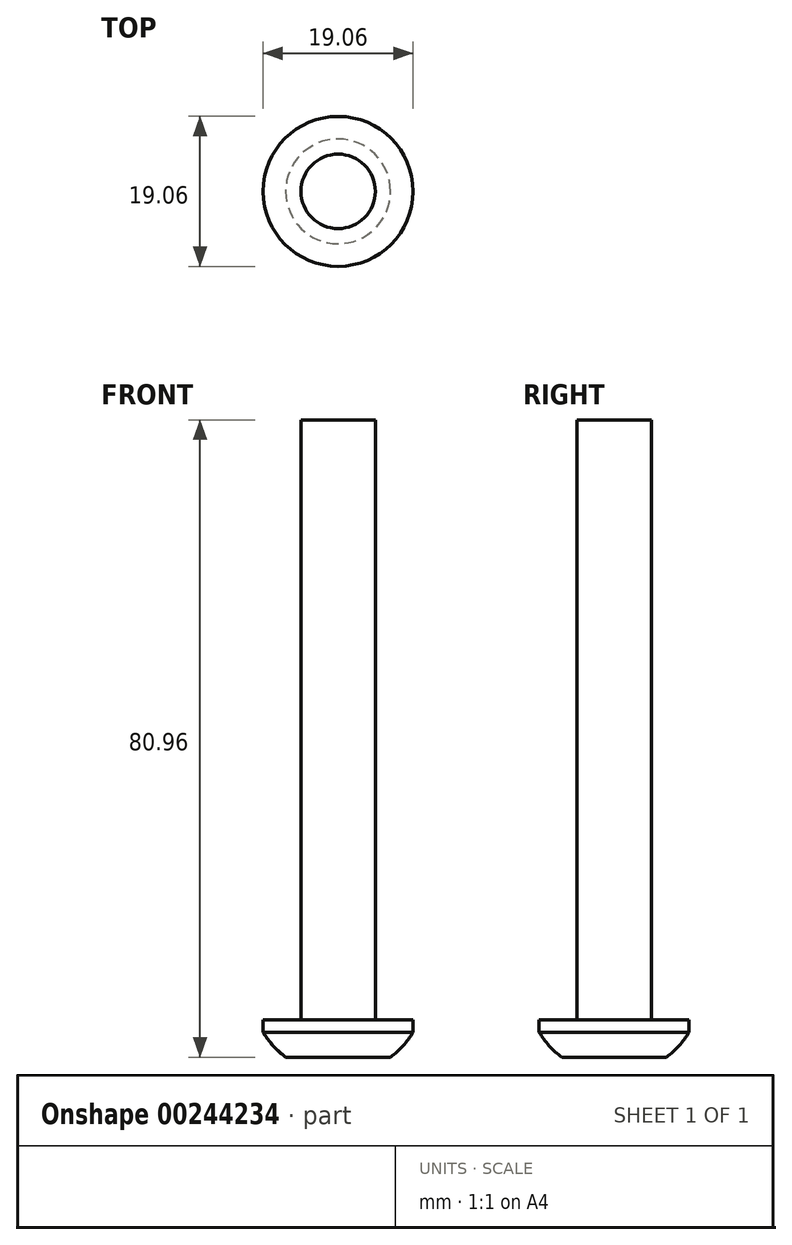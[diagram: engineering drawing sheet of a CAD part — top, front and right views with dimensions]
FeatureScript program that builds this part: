
annotation { "Feature Type Name" : "Feature", "Feature Type Description" : "" }
export const myFeature = defineFeature(function(context is Context, id is Id, definition is map)
    precondition{}
    {
        {
            var Q0;
            Q0=qCreatedBy(makeId("Front.planeOp"),FACE);
            var sketch = newSketch(context, id + "F0", { "sketchPlane" : qUnion([Q0])});
            skLineSegment(sketch, "E0", {"start": v(0, 0) * mm, "end": v(0, 76.2) * mm});
            skLineSegment(sketch, "E1", {"start": v(0, 76.2) * mm, "end": v(4.72, 76.2) * mm});
            skLineSegment(sketch, "E2", {"start": v(4.72, 76.2) * mm, "end": v(4.72, 0) * mm});
            skLineSegment(sketch, "E3", {"start": v(4.72, 0) * mm, "end": v(9.53, 0) * mm});
            skPoint(sketch, "E3.endSnap0", {"position": v(2.36, 0) * mm});
            skLineSegment(sketch, "E4", {"start": v(9.53, -1.59) * mm, "end": v(9.53, 0) * mm});
            skArc(sketch, "E5", {"start": v(9.53, -1.59) * mm, "mid": v(8.24, -3.31) * mm, "end": v(6.66, -4.76) * mm});
            skLineSegment(sketch, "E6", {"start": v(0, 0) * mm, "end": v(0, -4.76) * mm});
            skLineSegment(sketch, "E7", {"start": v(0, -4.76) * mm, "end": v(6.66, -4.76) * mm});
            skPoint(sketch, "E8.orphan", {"position": v(0, -6.98) * mm});
            skSolve(sketch);
        }
        {
            var Q0;
            Q0 = qSketchRegion(id + "F0", true);
            var Q1;
            Q1=sQuery(id+"F0.wireOp",EDGE,"E0");
            revolve(context, id + "F1", {"entities" : qUnion([Q0]), "axis" : qUnion([Q1]), "revolveType" : RevolveType.FULL});
        }
        {
            var Q0;
            Q0=makeQuery(id+"F1.opRevolve","SWEPT_FACE",FACE,{"disambiguationData":[OSD([sQuery(id+"F0.wireOp",EDGE,"E7")])]});
            var sketch = newSketch(context, id + "F2", { "sketchPlane" : qUnion([Q0])});
            skArc(sketch, "E9", {"start": v(5.27, 7.94) * mm, "mid": v(0, 9.53) * mm, "end": v(-5.27, 7.94) * mm});
            skLineSegment(sketch, "E10", {"start": v(0, 7.94) * mm, "end": v(5.27, 7.94) * mm});
            skLineSegment(sketch, "E11", {"start": v(0, 7.94) * mm, "end": v(-5.27, 7.94) * mm});
            skSolve(sketch);
        }
        {
            var Q0;
            Q0 = qSketchRegion(id + "F2", true);
            extrude(context, id + "F3", {"entities" : qUnion([Q0]), "operationType" : NewBodyOperationType.REMOVE, "oppositeDirection" : true, "depth" : 3 / 406.4 * mm});
        }
    });
